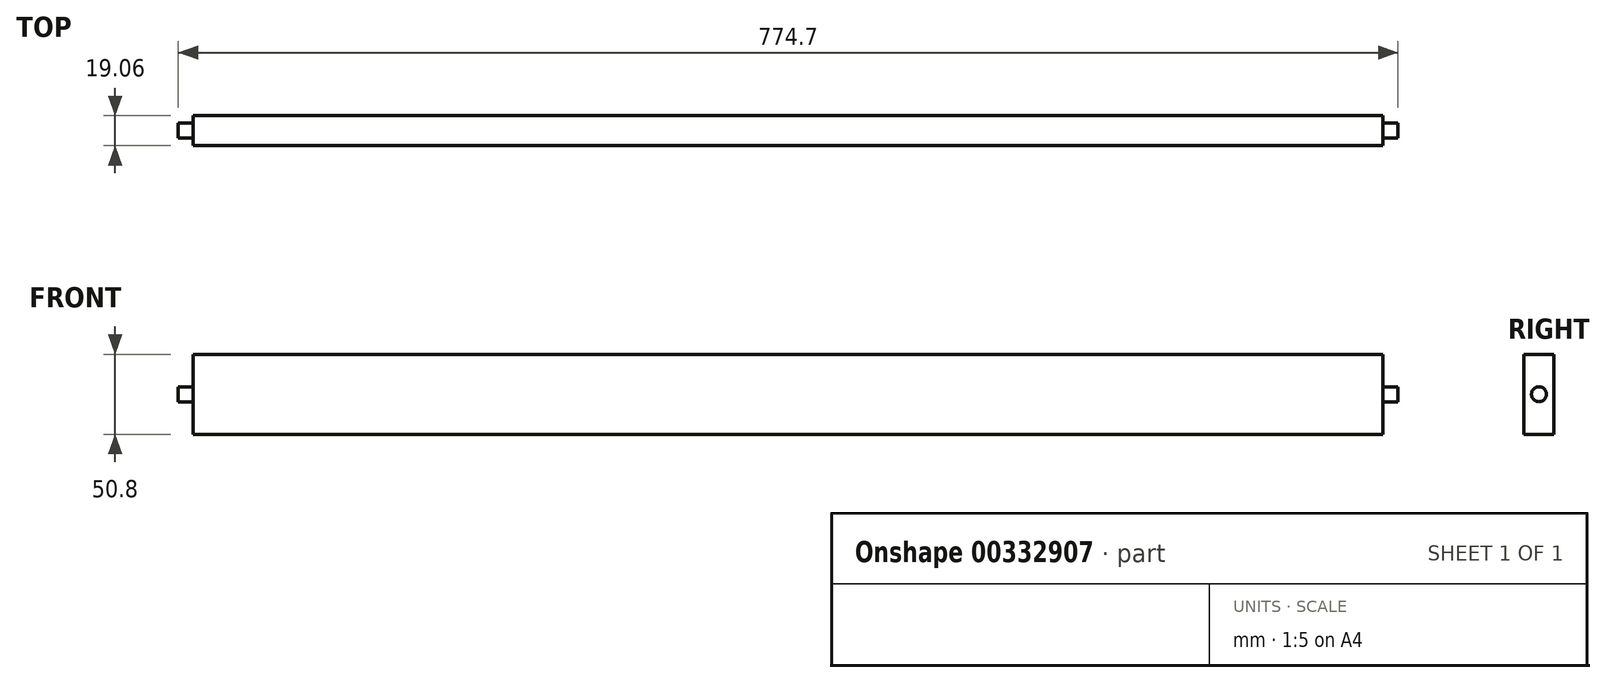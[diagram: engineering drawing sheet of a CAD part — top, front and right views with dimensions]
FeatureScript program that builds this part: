
annotation { "Feature Type Name" : "Feature", "Feature Type Description" : "" }
export const myFeature = defineFeature(function(context is Context, id is Id, definition is map)
    precondition{}
    {
        {
            var Q0;
            Q0=qCreatedBy(makeId("Top.planeOp"),FACE);
            var sketch = newSketch(context, id + "F0", { "sketchPlane" : qUnion([Q0])});
            skLineSegment(sketch, "E0.bottom", {"start": v(-377.83, -9.53) * mm, "end": v(377.83, -9.53) * mm});
            skLineSegment(sketch, "E0.top", {"start": v(-377.82, 9.53) * mm, "end": v(377.82, 9.53) * mm});
            skLineSegment(sketch, "E0.left", {"start": v(-377.83, -9.53) * mm, "end": v(-377.83, 9.52) * mm});
            skLineSegment(sketch, "E0.right", {"start": v(377.83, -9.53) * mm, "end": v(377.83, 9.52) * mm});
            skPoint(sketch, "E0.middle", {"position": v(0, 0) * mm});
            skSolve(sketch);
        }
        {
            var Q0;
            Q0=qSketchRegion(id+"F0",true);
            extrude(context, id + "F1", {"entities" : qUnion([Q0]), "depth" : 50.8 * mm});
        }
        {
            var Q0;
            Q0=qCreatedBy(makeId("Right.planeOp"),FACE);
            cPlane(context, id + "F2", {"entities" : qUnion([Q0]), "cplaneType" : CPlaneType.OFFSET, "offset" : 377.82 * mm, "width" : 152.4 * mm, "height" : 152.4 * mm});
        }
        {
            var Q0;
            Q0=qCreatedBy(id+"F2.planeOp",FACE);
            var sketch = newSketch(context, id + "F3", { "sketchPlane" : qUnion([Q0])});
            skCircle(sketch, "E1", {"center": v(0, 25.4) * mm, "radius": 4.76 * mm});
            skSolve(sketch);
        }
        {
            var Q0;
            Q0=qSketchRegion(id+"F3",true);
            extrude(context, id + "F4", {"entities" : qUnion([Q0]), "operationType" : NewBodyOperationType.ADD, "depth" : 9.52 * mm});
        }
        {
            var Q0;
            Q0=qCreatedBy(makeId("Right.planeOp"),FACE);
            cPlane(context, id + "F5", {"entities" : qUnion([Q0]), "cplaneType" : CPlaneType.OFFSET, "offset" : 377.82 * mm, "oppositeDirection" : true, "width" : 152.4 * mm, "height" : 152.4 * mm});
        }
        {
            var Q0;
            Q0=qCreatedBy(id+"F5.planeOp",FACE);
            var sketch = newSketch(context, id + "F6", { "sketchPlane" : qUnion([Q0])});
            skCircle(sketch, "E2", {"center": v(0, 25.42) * mm, "radius": 4.76 * mm});
            skSolve(sketch);
        }
        {
            var Q0;
            Q0=qSketchRegion(id+"F6",true);
            extrude(context, id + "F7", {"entities" : qUnion([Q0]), "operationType" : NewBodyOperationType.ADD, "oppositeDirection" : true, "depth" : 9.52 * mm});
        }
    });
